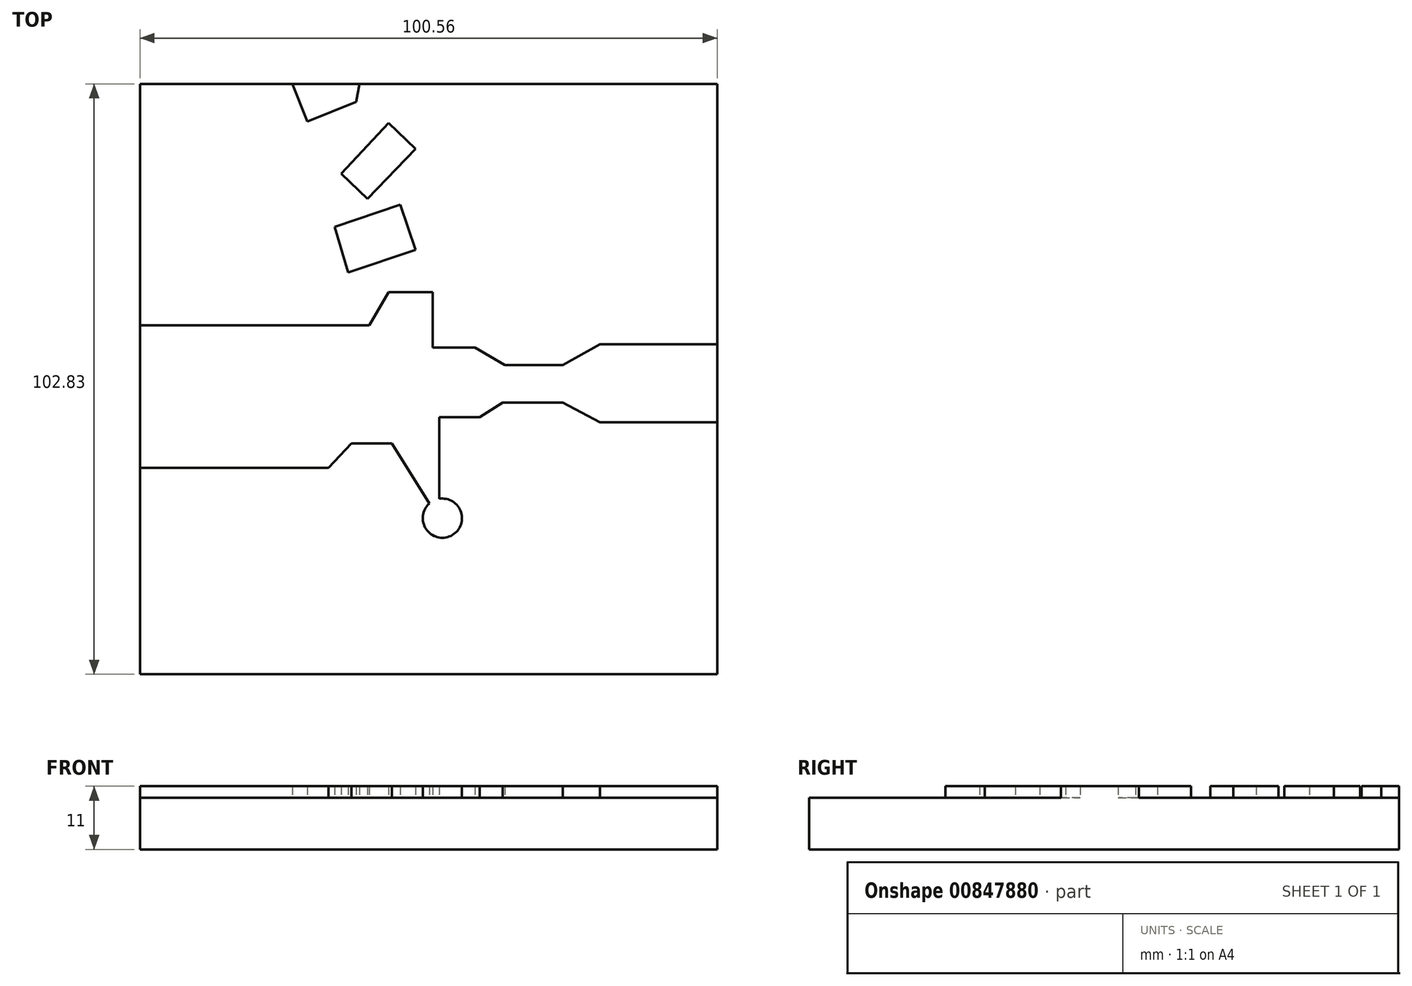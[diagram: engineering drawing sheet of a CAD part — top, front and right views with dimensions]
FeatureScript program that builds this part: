
annotation { "Feature Type Name" : "Feature", "Feature Type Description" : "" }
export const myFeature = defineFeature(function(context is Context, id is Id, definition is map)
    precondition{}
    {
        {
            var Q0;
            Q0=qCreatedBy(makeId("Top.planeOp"),FACE);
            var sketch = newSketch(context, id + "F0", { "sketchPlane" : qUnion([Q0])});
            skLineSegment(sketch, "E0.bottom", {"start": v(-48.01, 42.07) * mm, "end": v(52.55, 42.07) * mm});
            skLineSegment(sketch, "E0.top", {"start": v(-48.01, -60.76) * mm, "end": v(52.55, -60.76) * mm});
            skLineSegment(sketch, "E0.left", {"start": v(-48.01, 42.07) * mm, "end": v(-48.01, -60.76) * mm});
            skLineSegment(sketch, "E0.right", {"start": v(52.55, 42.07) * mm, "end": v(52.55, -60.76) * mm});
            skSolve(sketch);
        }
        {
            var Q0;
            Q0=makeQuery(id+"F0.imprint","IMPRINT",FACE,{"disambiguationData":[TD([[makeQuery(id+"F0.imprint","IMPRINT",EDGE,{"derivedFrom":sQuery(id+"F0.wireOp",EDGE,"E0.bottom")}),-1.0]])]});
            extrude(context, id + "F1", {"entities" : qUnion([Q0]), "depth" : 9 * mm, "offsetDistance" : 25 * mm});
        }
        {
            var Q0;
            Q0=makeQuery(id+"F1.opExtrude","CAP_FACE",FACE,{"disambiguationData":[OSD([sQuery(id+"F0.wireOp",EDGE,"E0.bottom"),sQuery(id+"F0.wireOp",EDGE,"E0.top"),sQuery(id+"F0.wireOp",EDGE,"E0.left"),sQuery(id+"F0.wireOp",EDGE,"E0.right")])],"isStart":false});
            var sketch = newSketch(context, id + "F2", { "sketchPlane" : qUnion([Q0])});
            skCircle(sketch, "E1", {"center": v(4.67, -33.57) * mm, "radius": 3.41 * mm});
            skSolve(sketch);
        }
        {
            var Q0;
            Q0=makeQuery(id+"F2.imprint","IMPRINT",FACE,{"disambiguationData":[TD([[makeQuery(id+"F2.imprint","IMPRINT",EDGE,{"derivedFrom":sQuery(id+"F2.wireOp",EDGE,"E1")}),1.0]])]});
            extrude(context, id + "F3", {"entities" : qUnion([Q0]), "operationType" : NewBodyOperationType.ADD, "depth" : 2 * mm, "offsetDistance" : 25 * mm});
        }
        {
            var Q0;
            Q0=makeQuery(id+"F1.opExtrude","CAP_FACE",FACE,{"disambiguationData":[OSD([sQuery(id+"F0.wireOp",EDGE,"E0.bottom"),sQuery(id+"F0.wireOp",EDGE,"E0.top"),sQuery(id+"F0.wireOp",EDGE,"E0.left"),sQuery(id+"F0.wireOp",EDGE,"E0.right")])],"isStart":false});
            var sketch = newSketch(context, id + "F4", { "sketchPlane" : qUnion([Q0])});
            skLineSegment(sketch, "E2", {"start": v(7.59, -35.34) * mm, "end": v(52.55, -60.76) * mm});
            skSolve(sketch);
        }
        {
            var Q0;
            Q0=sQuery(id+"F4.wireOp",EDGE,"E2");
            extrude(context, id + "F5", {"bodyType" : ToolBodyType.SURFACE, "surfaceEntities" : qUnion([Q0]), "depth" : 2 * mm, "offsetDistance" : 25 * mm});
        }
        {
            var Q0;
            Q0=makeQuery(id+"F1.opExtrude","CAP_FACE",FACE,{"disambiguationData":[OSD([sQuery(id+"F0.wireOp",EDGE,"E0.bottom"),sQuery(id+"F0.wireOp",EDGE,"E0.top"),sQuery(id+"F0.wireOp",EDGE,"E0.left"),sQuery(id+"F0.wireOp",EDGE,"E0.right")])],"isStart":false});
            var sketch = newSketch(context, id + "F6", { "sketchPlane" : qUnion([Q0])});
            skLineSegment(sketch, "E3", {"start": v(-48.01, -60.76) * mm, "end": v(1.43, -34.64) * mm});
            skSolve(sketch);
        }
        {
            var Q0;
            Q0=sQuery(id+"F6.wireOp",EDGE,"E3");
            extrude(context, id + "F7", {"bodyType" : ToolBodyType.SURFACE, "surfaceEntities" : qUnion([Q0]), "depth" : 2 * mm, "offsetDistance" : 25 * mm});
        }
        {
            var Q0;
            Q0=makeQuery(id+"F1.opExtrude","CAP_FACE",FACE,{"disambiguationData":[OSD([sQuery(id+"F0.wireOp",EDGE,"E0.bottom"),sQuery(id+"F0.wireOp",EDGE,"E0.top"),sQuery(id+"F0.wireOp",EDGE,"E0.left"),sQuery(id+"F0.wireOp",EDGE,"E0.right")])],"isStart":false});
            var sketch = newSketch(context, id + "F8", { "sketchPlane" : qUnion([Q0])});
            skLineSegment(sketch, "E4", {"start": v(2.4, -31.02) * mm, "end": v(-4.1, -20.54) * mm});
            skLineSegment(sketch, "E5", {"start": v(-4.1, -20.54) * mm, "end": v(-11.19, -20.54) * mm});
            skLineSegment(sketch, "E6", {"start": v(-11.19, -20.54) * mm, "end": v(-15.16, -24.79) * mm});
            skLineSegment(sketch, "E7", {"start": v(-15.16, -24.79) * mm, "end": v(-48.01, -24.79) * mm});
            skLineSegment(sketch, "E8", {"start": v(-48.01, -24.79) * mm, "end": v(-48.01, 0) * mm});
            skLineSegment(sketch, "E9", {"start": v(-48.01, 0) * mm, "end": v(-8.07, 0) * mm});
            skLineSegment(sketch, "E10", {"start": v(-8.07, 0) * mm, "end": v(-4.67, 5.8) * mm});
            skLineSegment(sketch, "E11", {"start": v(-4.67, 5.8) * mm, "end": v(2.97, 5.8) * mm});
            skLineSegment(sketch, "E12", {"start": v(2.97, 5.8) * mm, "end": v(2.97, -3.82) * mm});
            skLineSegment(sketch, "E13", {"start": v(2.97, -3.82) * mm, "end": v(10.34, -3.82) * mm});
            skLineSegment(sketch, "E14", {"start": v(10.34, -3.82) * mm, "end": v(15.58, -6.9) * mm});
            skLineSegment(sketch, "E15", {"start": v(15.58, -6.9) * mm, "end": v(25.64, -6.9) * mm});
            skLineSegment(sketch, "E16", {"start": v(25.64, -6.9) * mm, "end": v(32.15, -3.26) * mm});
            skLineSegment(sketch, "E17", {"start": v(32.15, -3.26) * mm, "end": v(52.55, -3.26) * mm});
            skLineSegment(sketch, "E18", {"start": v(52.55, -3.26) * mm, "end": v(52.55, -16.85) * mm});
            skLineSegment(sketch, "E19", {"start": v(52.55, -16.85) * mm, "end": v(32.15, -16.85) * mm});
            skLineSegment(sketch, "E20", {"start": v(32.15, -16.85) * mm, "end": v(25.64, -13.46) * mm});
            skLineSegment(sketch, "E21", {"start": v(25.64, -13.46) * mm, "end": v(15.16, -13.46) * mm});
            skLineSegment(sketch, "E22", {"start": v(15.16, -13.46) * mm, "end": v(11.19, -16) * mm});
            skLineSegment(sketch, "E23", {"start": v(11.19, -16) * mm, "end": v(4.1, -16) * mm});
            skLineSegment(sketch, "E24", {"start": v(4.1, -16) * mm, "end": v(4.1, -30.2) * mm});
            skSolve(sketch);
        }
        {
            var Q0;
            {var subQ0=sQuery(id+"F8.wireOp",EDGE,"E4");Q0=makeQuery(id+"F8.imprint","IMPRINT",FACE,{"disambiguationData":[TD([[makeQuery(id+"F8.imprint","IMPRINT",EDGE,{"derivedFrom":subQ0}),-1.0]])]});}
            extrude(context, id + "F9", {"entities" : qUnion([Q0]), "operationType" : NewBodyOperationType.ADD, "depth" : 2 * mm, "offsetDistance" : 25 * mm});
        }
        {
            var Q0;
            {var subQ0=sQuery(id+"F2.wireOp",EDGE,"E1");Q0=makeQuery(id+"F9.boolean.opBoolean","MERGE",FACE,{"derivedFrom":[makeQuery(id+"F3.opExtrude","CAP_FACE",FACE,{"disambiguationData":[OSD([subQ0])],"isStart":false}),makeQuery(id+"F9.opExtrude","CAP_FACE",FACE,{"disambiguationData":[OSD([subQ0,sQuery(id+"F8.wireOp",EDGE,"E4"),sQuery(id+"F8.wireOp",EDGE,"E5"),sQuery(id+"F8.wireOp",EDGE,"E6"),sQuery(id+"F8.wireOp",EDGE,"E7"),sQuery(id+"F8.wireOp",EDGE,"E8"),sQuery(id+"F8.wireOp",EDGE,"E9"),sQuery(id+"F8.wireOp",EDGE,"E10"),sQuery(id+"F8.wireOp",EDGE,"E11"),sQuery(id+"F8.wireOp",EDGE,"E12"),sQuery(id+"F8.wireOp",EDGE,"E13"),sQuery(id+"F8.wireOp",EDGE,"E14"),sQuery(id+"F8.wireOp",EDGE,"E15"),sQuery(id+"F8.wireOp",EDGE,"E16"),sQuery(id+"F8.wireOp",EDGE,"E17"),sQuery(id+"F8.wireOp",EDGE,"E18"),sQuery(id+"F8.wireOp",EDGE,"E19"),sQuery(id+"F8.wireOp",EDGE,"E20"),sQuery(id+"F8.wireOp",EDGE,"E21"),sQuery(id+"F8.wireOp",EDGE,"E22"),sQuery(id+"F8.wireOp",EDGE,"E23"),sQuery(id+"F8.wireOp",EDGE,"E24")])],"isStart":false})]});}
            var sketch = newSketch(context, id + "F10", { "sketchPlane" : qUnion([Q0])});
            skLineSegment(sketch, "E25", {"start": v(-39.8, -6.66) * mm, "end": v(-10.62, -6.66) * mm});
            skSolve(sketch);
        }
        {
            var Q0;
            Q0=sQuery(id+"F10.wireOp",EDGE,"E25");
            extrude(context, id + "F11", {"bodyType" : ToolBodyType.SURFACE, "surfaceEntities" : qUnion([Q0]), "oppositeDirection" : true, "depth" : 2 * mm, "offsetDistance" : 25 * mm});
        }
        {
            var Q0;
            {var subQ0=sQuery(id+"F2.wireOp",EDGE,"E1");Q0=makeQuery(id+"F9.boolean.opBoolean","MERGE",FACE,{"derivedFrom":[makeQuery(id+"F3.opExtrude","CAP_FACE",FACE,{"disambiguationData":[OSD([subQ0])],"isStart":false}),makeQuery(id+"F9.opExtrude","CAP_FACE",FACE,{"disambiguationData":[OSD([subQ0,sQuery(id+"F8.wireOp",EDGE,"E4"),sQuery(id+"F8.wireOp",EDGE,"E5"),sQuery(id+"F8.wireOp",EDGE,"E6"),sQuery(id+"F8.wireOp",EDGE,"E7"),sQuery(id+"F8.wireOp",EDGE,"E8"),sQuery(id+"F8.wireOp",EDGE,"E9"),sQuery(id+"F8.wireOp",EDGE,"E10"),sQuery(id+"F8.wireOp",EDGE,"E11"),sQuery(id+"F8.wireOp",EDGE,"E12"),sQuery(id+"F8.wireOp",EDGE,"E13"),sQuery(id+"F8.wireOp",EDGE,"E14"),sQuery(id+"F8.wireOp",EDGE,"E15"),sQuery(id+"F8.wireOp",EDGE,"E16"),sQuery(id+"F8.wireOp",EDGE,"E17"),sQuery(id+"F8.wireOp",EDGE,"E18"),sQuery(id+"F8.wireOp",EDGE,"E19"),sQuery(id+"F8.wireOp",EDGE,"E20"),sQuery(id+"F8.wireOp",EDGE,"E21"),sQuery(id+"F8.wireOp",EDGE,"E22"),sQuery(id+"F8.wireOp",EDGE,"E23"),sQuery(id+"F8.wireOp",EDGE,"E24")])],"isStart":false})]});}
            var sketch = newSketch(context, id + "F12", { "sketchPlane" : qUnion([Q0])});
            skLineSegment(sketch, "E26", {"start": v(5.04, -6.28) * mm, "end": v(5.04, -12.4) * mm});
            skSolve(sketch);
        }
        {
            var Q0;
            Q0=sQuery(id+"F12.wireOp",EDGE,"E26");
            extrude(context, id + "F13", {"bodyType" : ToolBodyType.SURFACE, "surfaceEntities" : qUnion([Q0]), "oppositeDirection" : true, "depth" : 2 * mm, "offsetDistance" : 25 * mm});
        }
        {
            var Q0;
            {var subQ0=sQuery(id+"F2.wireOp",EDGE,"E1");Q0=makeQuery(id+"F9.boolean.opBoolean","MERGE",FACE,{"derivedFrom":[makeQuery(id+"F3.opExtrude","CAP_FACE",FACE,{"disambiguationData":[OSD([subQ0])],"isStart":false}),makeQuery(id+"F9.opExtrude","CAP_FACE",FACE,{"disambiguationData":[OSD([subQ0,sQuery(id+"F8.wireOp",EDGE,"E4"),sQuery(id+"F8.wireOp",EDGE,"E5"),sQuery(id+"F8.wireOp",EDGE,"E6"),sQuery(id+"F8.wireOp",EDGE,"E7"),sQuery(id+"F8.wireOp",EDGE,"E8"),sQuery(id+"F8.wireOp",EDGE,"E9"),sQuery(id+"F8.wireOp",EDGE,"E10"),sQuery(id+"F8.wireOp",EDGE,"E11"),sQuery(id+"F8.wireOp",EDGE,"E12"),sQuery(id+"F8.wireOp",EDGE,"E13"),sQuery(id+"F8.wireOp",EDGE,"E14"),sQuery(id+"F8.wireOp",EDGE,"E15"),sQuery(id+"F8.wireOp",EDGE,"E16"),sQuery(id+"F8.wireOp",EDGE,"E17"),sQuery(id+"F8.wireOp",EDGE,"E18"),sQuery(id+"F8.wireOp",EDGE,"E19"),sQuery(id+"F8.wireOp",EDGE,"E20"),sQuery(id+"F8.wireOp",EDGE,"E21"),sQuery(id+"F8.wireOp",EDGE,"E22"),sQuery(id+"F8.wireOp",EDGE,"E23"),sQuery(id+"F8.wireOp",EDGE,"E24")])],"isStart":false})]});}
            var sketch = newSketch(context, id + "F14", { "sketchPlane" : qUnion([Q0])});
            skLineSegment(sketch, "E27", {"start": v(8.14, -6.38) * mm, "end": v(8.14, -12.5) * mm});
            skSolve(sketch);
        }
        {
            var Q0;
            Q0=sQuery(id+"F14.wireOp",EDGE,"E27");
            extrude(context, id + "F15", {"bodyType" : ToolBodyType.SURFACE, "surfaceEntities" : qUnion([Q0]), "oppositeDirection" : true, "depth" : 2 * mm, "offsetDistance" : 25 * mm});
        }
        {
            var Q0;
            {var subQ0=sQuery(id+"F0.wireOp",EDGE,"E0.bottom");var subQ1=sQuery(id+"F0.wireOp",EDGE,"E0.right");var subQ2=sQuery(id+"F0.wireOp",EDGE,"E0.left");Q0=makeQuery(id+"F9.boolean.opBoolean","SPLIT",FACE,{"disambiguationData":[TD([makeQuery(id+"F1.opExtrude","SWEPT_FACE",FACE,{"disambiguationData":[OSD([subQ0])]})])],"derivedFrom":makeQuery(id+"F1.opExtrude","CAP_FACE",FACE,{"disambiguationData":[OSD([subQ0,sQuery(id+"F0.wireOp",EDGE,"E0.top"),subQ2,subQ1])],"isStart":false})});}
            var sketch = newSketch(context, id + "F16", { "sketchPlane" : qUnion([Q0])});
            skLineSegment(sketch, "E28", {"start": v(-11.76, 9.2) * mm, "end": v(0, 13.17) * mm});
            skLineSegment(sketch, "E29", {"start": v(0, 13.17) * mm, "end": v(-2.65, 21.03) * mm});
            skLineSegment(sketch, "E30", {"start": v(-2.65, 21.03) * mm, "end": v(-14.12, 17.16) * mm});
            skLineSegment(sketch, "E31", {"start": v(-14.12, 17.16) * mm, "end": v(-11.76, 9.2) * mm});
            skSolve(sketch);
        }
        {
            var Q0;
            Q0=makeQuery(id+"F16.imprint","IMPRINT",FACE,{"disambiguationData":[TD([[makeQuery(id+"F16.imprint","IMPRINT",EDGE,{"derivedFrom":sQuery(id+"F16.wireOp",EDGE,"E28")}),1.0]])]});
            extrude(context, id + "F17", {"entities" : qUnion([Q0]), "operationType" : NewBodyOperationType.ADD, "depth" : 2 * mm, "offsetDistance" : 25 * mm});
        }
        {
            var Q0;
            {var subQ0=sQuery(id+"F0.wireOp",EDGE,"E0.bottom");var subQ1=sQuery(id+"F0.wireOp",EDGE,"E0.right");var subQ2=sQuery(id+"F0.wireOp",EDGE,"E0.left");Q0=makeQuery(id+"F9.boolean.opBoolean","SPLIT",FACE,{"disambiguationData":[TD([makeQuery(id+"F1.opExtrude","SWEPT_FACE",FACE,{"disambiguationData":[OSD([subQ0])]})])],"derivedFrom":makeQuery(id+"F1.opExtrude","CAP_FACE",FACE,{"disambiguationData":[OSD([subQ0,sQuery(id+"F0.wireOp",EDGE,"E0.top"),subQ2,subQ1])],"isStart":false})});}
            var sketch = newSketch(context, id + "F18", { "sketchPlane" : qUnion([Q0])});
            skLineSegment(sketch, "E32", {"start": v(-4.67, 35.27) * mm, "end": v(0, 30.74) * mm});
            skLineSegment(sketch, "E33", {"start": v(0, 30.74) * mm, "end": v(-8.41, 22.06) * mm});
            skLineSegment(sketch, "E34", {"start": v(-8.41, 22.06) * mm, "end": v(-12.93, 26.44) * mm});
            skLineSegment(sketch, "E35", {"start": v(-12.93, 26.44) * mm, "end": v(-4.67, 35.27) * mm});
            skSolve(sketch);
        }
        {
            var Q0;
            Q0=makeQuery(id+"F18.imprint","IMPRINT",FACE,{"disambiguationData":[TD([[makeQuery(id+"F18.imprint","IMPRINT",EDGE,{"derivedFrom":sQuery(id+"F18.wireOp",EDGE,"E32")}),-1.0]])]});
            extrude(context, id + "F19", {"entities" : qUnion([Q0]), "operationType" : NewBodyOperationType.ADD, "depth" : 2 * mm, "offsetDistance" : 25 * mm});
        }
        {
            var Q0;
            {var subQ0=sQuery(id+"F0.wireOp",EDGE,"E0.bottom");var subQ1=sQuery(id+"F0.wireOp",EDGE,"E0.right");var subQ2=sQuery(id+"F0.wireOp",EDGE,"E0.left");Q0=makeQuery(id+"F9.boolean.opBoolean","SPLIT",FACE,{"disambiguationData":[TD([makeQuery(id+"F1.opExtrude","SWEPT_FACE",FACE,{"disambiguationData":[OSD([subQ0])]})])],"derivedFrom":makeQuery(id+"F1.opExtrude","CAP_FACE",FACE,{"disambiguationData":[OSD([subQ0,sQuery(id+"F0.wireOp",EDGE,"E0.top"),subQ2,subQ1])],"isStart":false})});}
            var sketch = newSketch(context, id + "F20", { "sketchPlane" : qUnion([Q0])});
            skLineSegment(sketch, "E36", {"start": v(-10.34, 38.95) * mm, "end": v(-18.84, 35.55) * mm});
            skLineSegment(sketch, "E37", {"start": v(-18.84, 35.55) * mm, "end": v(-21.44, 42.07) * mm});
            skLineSegment(sketch, "E38", {"start": v(-21.44, 42.07) * mm, "end": v(-9.77, 42.07) * mm});
            skLineSegment(sketch, "E39", {"start": v(-9.77, 42.07) * mm, "end": v(-10.34, 38.95) * mm});
            skSolve(sketch);
        }
        {
            var Q0;
            Q0=makeQuery(id+"F20.imprint","IMPRINT",FACE,{"disambiguationData":[TD([[makeQuery(id+"F20.imprint","IMPRINT",EDGE,{"derivedFrom":sQuery(id+"F20.wireOp",EDGE,"E36")}),-1.0]])]});
            extrude(context, id + "F21", {"entities" : qUnion([Q0]), "operationType" : NewBodyOperationType.ADD, "depth" : 2 * mm, "offsetDistance" : 25 * mm});
        }
    });
